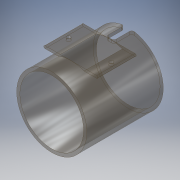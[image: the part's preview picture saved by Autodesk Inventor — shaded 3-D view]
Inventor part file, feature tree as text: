
AUTODESK INVENTOR PART (.ipt)
format: ipt  version: 2019 (Build 230136000, 136)  size: 209,920 bytes
history: native  units: mm
features: extrude x4, sketch x4, projected_geometry x2, plane x1, mirror x1, fillet x1
ambient origin geometry x8: Origin, YZ Plane, XZ Plane, XY Plane, X Axis, Y Axis, Z Axis, Center Point
bodies: Solid1 (feature_tree)
feature tree (13):
  extrude  "Extrusion1"  Depth=100.0mm
  extrude  "Extrusion2"  Depth=30.0mm TaperAngle=0.0deg
  plane  "Work Plane1"
  extrude  "Extrusion3"  Depth=7.0mm TaperAngle=0.0deg
  mirror  "Mirror2"
  fillet  "Fillet1"  Radius=12.0mm
  extrude  "Extrusion4"  Depth=4.0mm
  sketch  "Sketch1"  dims[d0=110.0mm d1=100.0mm]
  sketch  "Sketch2"  dims[d19=120.0mm d20=0.0mm d21=30.0mm d22=0.0mm]
  sketch  "Sketch3"  dims[d23=-60.0mm d27=7.0mm d28=0.0mm d33=12.0mm]
  projected_geometry  "Projected Loop6"
  sketch  "Sketch4"  dims[d43=12.0mm d44=29.0mm d45=4.0mm d46=4.0mm d48=6.0mm d49=5.0mm d50=0.0mm d51=6.0mm]
  projected_geometry  "Projected Loop7"
